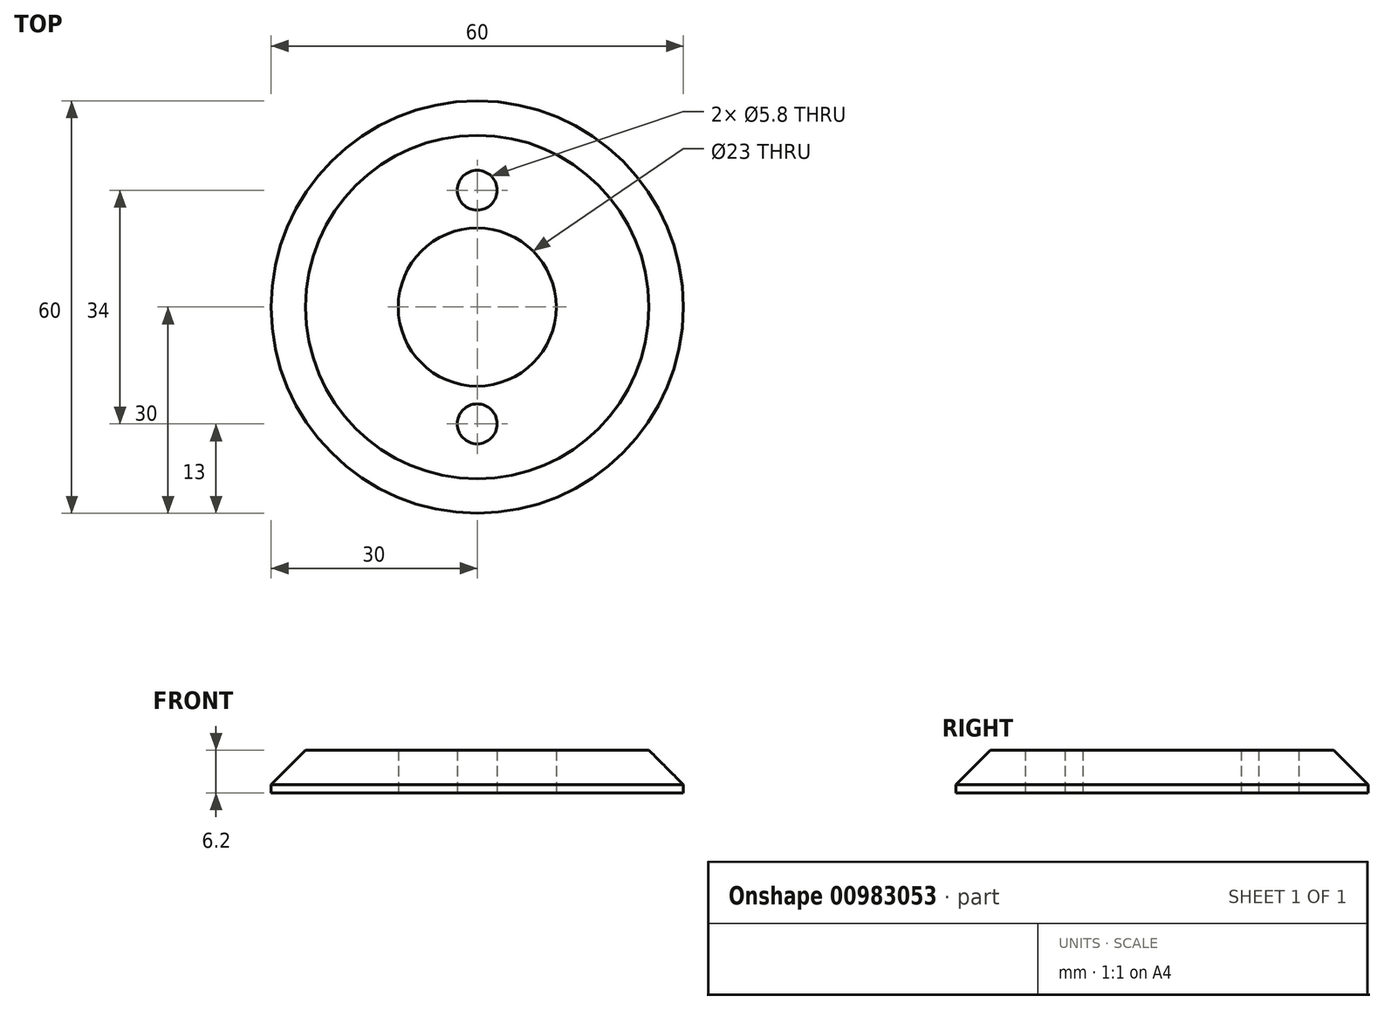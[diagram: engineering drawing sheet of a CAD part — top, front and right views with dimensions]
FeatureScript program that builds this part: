
annotation { "Feature Type Name" : "Feature", "Feature Type Description" : "" }
export const myFeature = defineFeature(function(context is Context, id is Id, definition is map)
    precondition{}
    {
        {
            var Q0;
            Q0=qCreatedBy(makeId("Top.planeOp"),FACE);
            var sketch = newSketch(context, id + "F0", { "sketchPlane" : qUnion([Q0])});
            skCircle(sketch, "E0", {"center": v(0, 0) * mm, "radius": 30 * mm});
            skCircle(sketch, "E1", {"center": v(0, 0) * mm, "radius": 11.5 * mm});
            skCircle(sketch, "E2", {"center": v(0, 17) * mm, "radius": 2.9 * mm});
            skCircle(sketch, "E3", {"center": v(0, -17) * mm, "radius": 2.9 * mm});
            skSolve(sketch);
        }
        {
            var Q0;
            Q0 = qSketchRegion(id + "F0", true);
            extrude(context, id + "F1", {"entities" : qUnion([Q0]), "depth" : 6.2 * mm, "offsetDistance" : 25 * mm});
        }
        {
            var Q0;
            Q0=makeQuery(id+"F1.opExtrude","CAP_EDGE",EDGE,{"disambiguationData":[OSD([sQuery(id+"F0.wireOp",EDGE,"E0")])],"isStart":false});
            chamfer(context, id + "F2", {"entities" : qUnion([Q0]), "width" : 5 * mm, "tangentPropagation" : true});
        }
    });
